# Revit family: Дверь антивандальная внутриподъездная для этажной ниши связи ССД
name_source: partatom
category: Электрооборудование
revit_build: Autodesk Revit 2018 (Build: 20170927_1515(x64)
units: mm (PartAtom-declared; Revit-internal decimal feet)

## family parameters
Общий = Нет
Основа = Грань
При загрузке вырезать с полостями = Да
Размер круглого соединителя = Использовать диаметр
Тип детали = Другая панель
Точка расчета площади = Нет

## types (1)
- Дверь антивандальная внутриподъездная для этажной ниши связи
    Дверь КП МПТЦ_LOD200 = КП МПТЦ  ССД_LOD 200 : ШТ-НСс 2 ССД_LOD 200
    Комплектность = Дверь в сборе	1 шт.
Кронштейн	6 шт.
Растяжка	3 шт.
Комплект ключей	1 шт.
Комплект метизов	1 шт.
Анкерный болт	9 шт.
    Описание изделия = Дверь антивандальная внутриподъездная 
предназначена для ограничения доступа к
оборудованию связи в бетонной нише зданий 
с размерами (ШхГхВ) 1000х400х2100.
    Отметка по умолчанию = 500 мм
    Размеры (ШхГхВ), мм = 1000х400х2100
    Спец.ЕдИзм = шт.
    Спец.Изготовитель = ЗАО "СвязьСтройДеталь"
    Спец.КодОборудИзделияМатериала = 130411-01583
    Спец.Количество = 1
    Спец.НаименованиеИТехнХар = Дверь антивандальная внутриподъездная для этажной ниши связи
    Спец.Подраздел = Шкафы подъездные
    Спец.РазделСпец = Шкафы и стойки телекоммуникационные
    Спец.ТипМаркаОбозначДокумента = КП МПТЦ
    Ссылка на инструкцию изделия = https://www.ssd.ru
    Ссылка на сайт производителя = https://www.ssd.ru
    Характеристики = Материал - Листовая сталь
Эмаль порошковая -RAL 7035
Тип конструкции - Сборно-разборная
Тип вентиляции - Жалюзи вентиляционные
Размеры прохода в двери, мм - 2064х931
Масса, кг -73,6
